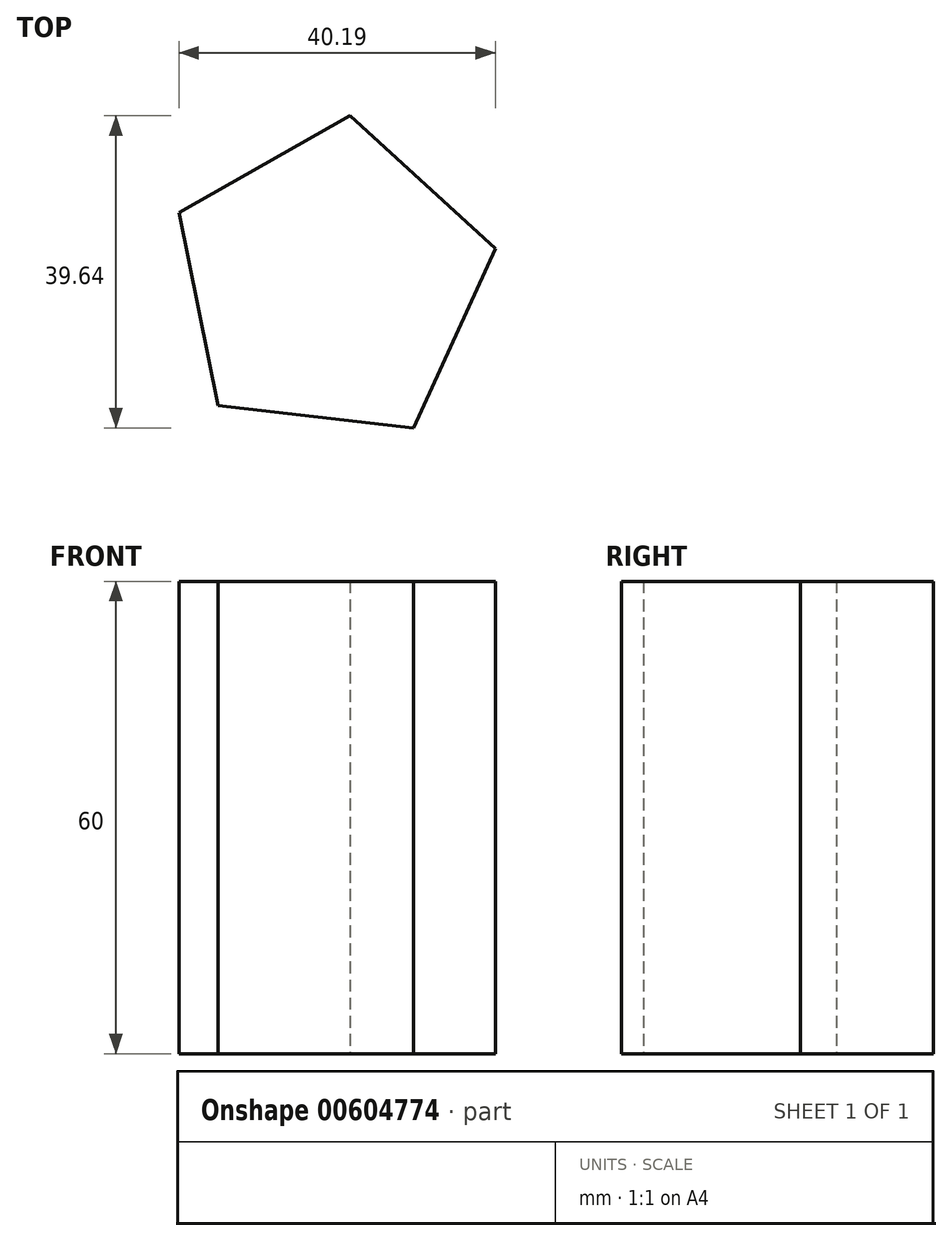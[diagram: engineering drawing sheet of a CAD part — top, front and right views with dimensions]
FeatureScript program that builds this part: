
annotation { "Feature Type Name" : "Feature", "Feature Type Description" : "" }
export const myFeature = defineFeature(function(context is Context, id is Id, definition is map)
    precondition{}
    {
        {
            var Q0;
            Q0=qCreatedBy(makeId("Top.planeOp"),FACE);
            var sketch = newSketch(context, id + "F0", { "sketchPlane" : qUnion([Q0])});
            skCircle(sketch, "E0.cCircle", {"center": v(0, 0) * mm, "radius": 21.27 * mm, "construction": true});
            skLineSegment(sketch, "E0.0", {"start": v(10.47, -18.5) * mm, "end": v(-14.37, -15.68) * mm});
            skLineSegment(sketch, "E0.1", {"start": v(-14.37, -15.68) * mm, "end": v(-19.35, 8.82) * mm});
            skLineSegment(sketch, "E0.2", {"start": v(-19.35, 8.82) * mm, "end": v(2.4, 21.13) * mm});
            skLineSegment(sketch, "E0.3", {"start": v(2.4, 21.13) * mm, "end": v(20.84, 4.24) * mm});
            skLineSegment(sketch, "E0.4", {"start": v(20.84, 4.24) * mm, "end": v(10.47, -18.5) * mm});
            skSolve(sketch);
        }
        {
            var Q0;
            Q0 = qSketchRegion(id + "F0", true);
            extrude(context, id + "F1", {"entities" : qUnion([Q0]), "depth" : 60 * mm, "offsetDistance" : 25.4 * mm});
        }
    });
